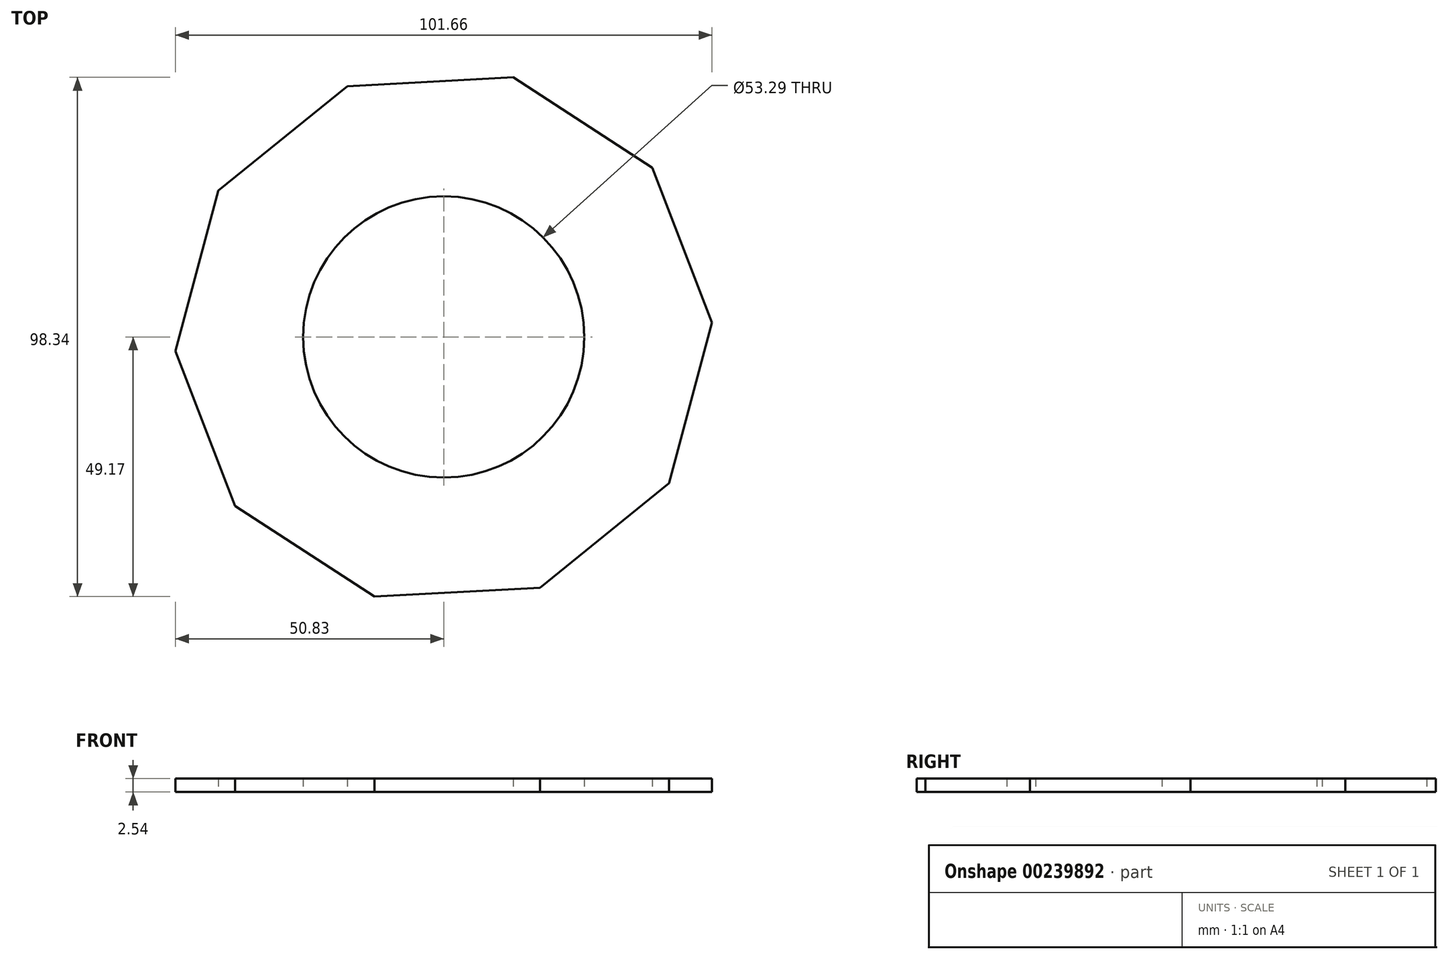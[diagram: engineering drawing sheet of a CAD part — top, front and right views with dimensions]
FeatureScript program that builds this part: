
annotation { "Feature Type Name" : "Feature", "Feature Type Description" : "" }
export const myFeature = defineFeature(function(context is Context, id is Id, definition is map)
    precondition{}
    {
        {
            var Q0;
            Q0=qCreatedBy(makeId("Top.planeOp"),FACE);
            var sketch = newSketch(context, id + "F0", { "sketchPlane" : qUnion([Q0])});
            skCircle(sketch, "E0.cCircle", {"center": v(0, 0) * mm, "radius": 50.9 * mm, "construction": true});
            skLineSegment(sketch, "E0.0", {"start": v(-18.26, 47.51) * mm, "end": v(13.15, 49.17) * mm});
            skLineSegment(sketch, "E0.1", {"start": v(13.15, 49.17) * mm, "end": v(39.54, 32.05) * mm});
            skLineSegment(sketch, "E0.2", {"start": v(39.54, 32.05) * mm, "end": v(50.83, 2.69) * mm});
            skLineSegment(sketch, "E0.3", {"start": v(50.83, 2.69) * mm, "end": v(42.7, -27.7) * mm});
            skLineSegment(sketch, "E0.4", {"start": v(42.7, -27.7) * mm, "end": v(18.26, -47.51) * mm});
            skLineSegment(sketch, "E0.5", {"start": v(18.26, -47.51) * mm, "end": v(-13.15, -49.17) * mm});
            skLineSegment(sketch, "E0.6", {"start": v(-13.15, -49.17) * mm, "end": v(-39.54, -32.05) * mm});
            skLineSegment(sketch, "E0.7", {"start": v(-39.54, -32.05) * mm, "end": v(-50.83, -2.69) * mm});
            skLineSegment(sketch, "E0.8", {"start": v(-50.83, -2.69) * mm, "end": v(-42.7, 27.7) * mm});
            skLineSegment(sketch, "E0.9", {"start": v(-42.7, 27.7) * mm, "end": v(-18.26, 47.51) * mm});
            skSolve(sketch);
        }
        {
            var Q0;
            Q0=makeQuery(id+"F0.imprint","IMPRINT",FACE,{"disambiguationData":[TD([[makeQuery(id+"F0.imprint","IMPRINT",EDGE,{"derivedFrom":sQuery(id+"F0.wireOp",EDGE,"E0.0")}),-1.0]])]});
            var sketch = newSketch(context, id + "F1", { "sketchPlane" : qUnion([Q0])});
            skCircle(sketch, "E1", {"center": v(0, 0) * mm, "radius": 26.92 * mm});
            skSolve(sketch);
        }
        {
            var Q0;
            Q0=sQuery(id+"F1.wireOp",EDGE,"E1");
            extrude(context, id + "F2", {"bodyType" : ToolBodyType.SURFACE, "surfaceEntities" : qUnion([Q0]), "depth" : 69.85 * mm});
        }
        {
            var Q0;
            Q0 = qSketchRegion(id + "F0", true);
            extrude(context, id + "F3", {"entities" : qUnion([Q0]), "depth" : 2.54 * mm});
        }
        {
            var Q0;
            Q0=makeQuery(id+"F3.opExtrude","CAP_FACE",FACE,{"disambiguationData":[OSD([sQuery(id+"F0.wireOp",EDGE,"E0.0"),sQuery(id+"F0.wireOp",EDGE,"E0.1"),sQuery(id+"F0.wireOp",EDGE,"E0.2"),sQuery(id+"F0.wireOp",EDGE,"E0.3"),sQuery(id+"F0.wireOp",EDGE,"E0.4"),sQuery(id+"F0.wireOp",EDGE,"E0.5"),sQuery(id+"F0.wireOp",EDGE,"E0.6"),sQuery(id+"F0.wireOp",EDGE,"E0.7"),sQuery(id+"F0.wireOp",EDGE,"E0.8"),sQuery(id+"F0.wireOp",EDGE,"E0.9")])],"isStart":true});
            var sketch = newSketch(context, id + "F4", { "sketchPlane" : qUnion([Q0])});
            skCircle(sketch, "E2", {"center": v(0, 0) * mm, "radius": 26.65 * mm});
            skSolve(sketch);
        }
        {
            var Q0;
            Q0 = qSketchRegion(id + "F4", true);
            extrude(context, id + "F5", {"entities" : qUnion([Q0]), "operationType" : NewBodyOperationType.REMOVE, "oppositeDirection" : true, "depth" : 25.4 * mm});
        }
    });
